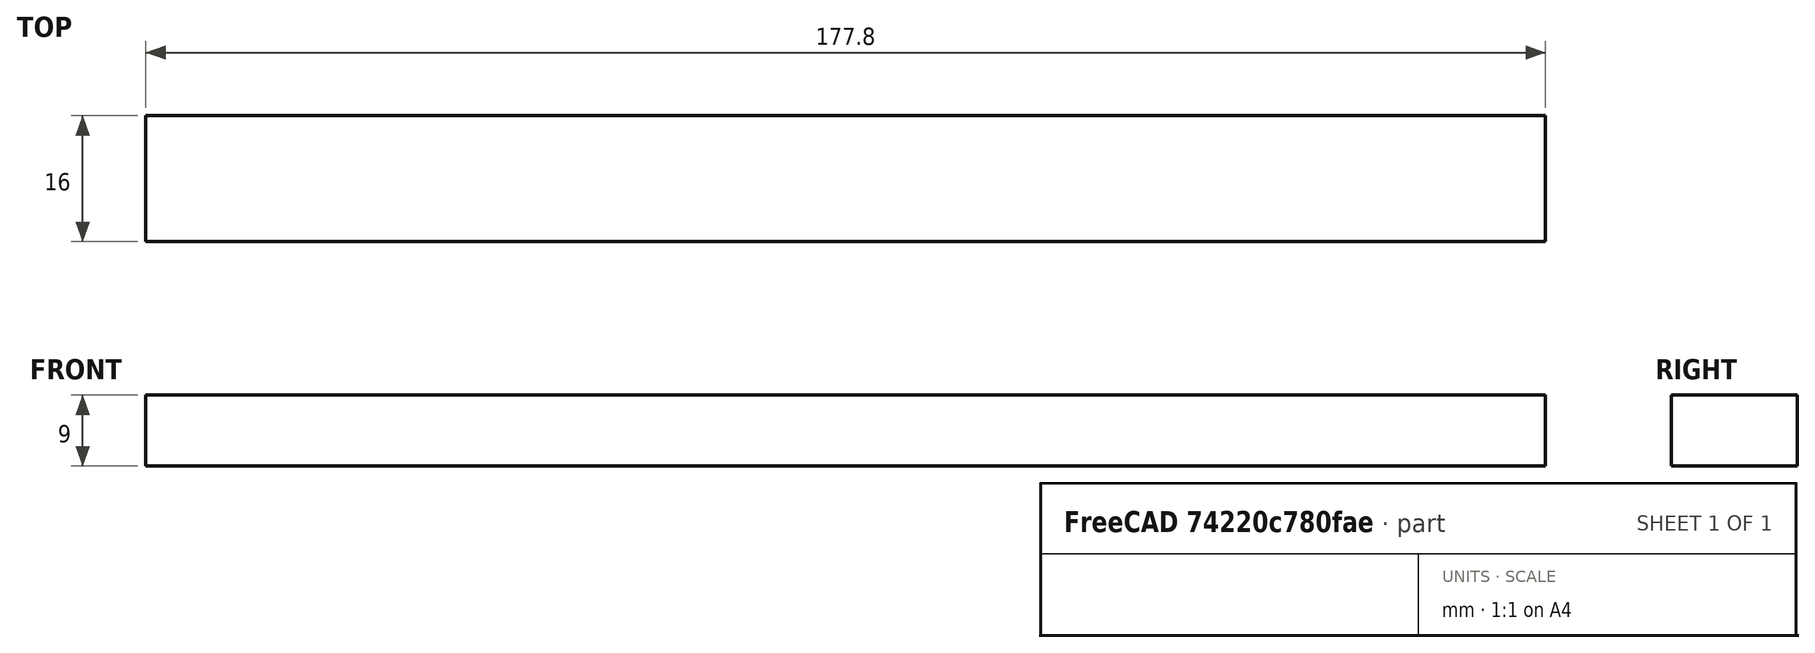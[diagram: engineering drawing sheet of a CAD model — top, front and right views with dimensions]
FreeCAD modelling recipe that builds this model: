
FCSTD DOCUMENT  (FreeCAD 0.17R13543 (Git))
Label: prop_dummy
License: All rights reserved
LicenseURL: http://en.wikipedia.org/wiki/All_rights_reserved
objects: Sketcher::SketchObject×1, PartDesign::Pad×1, PartDesign::Body×1, App::Part×1
note: 4 computed .brp shape members not serialized (recipe doc carries the construction recipe); baked Part::Feature solids carry a one-line shape summary decoded from their .brp

FEATURE [Sketcher::SketchObject] Sketch
  MapMode = 5
  Placement = pos=(0,0,0) rot=(1,0,0;1.5708rad)
  Support = -> [XZ_Plane001]
  sketch-geometry (4):
    g0: LineSegment StartX=-88.9 StartY=-8 StartZ=0 EndX=88.9 EndY=-8 EndZ=0
    g1: LineSegment StartX=88.9 StartY=-8 StartZ=0 EndX=88.9 EndY=8 EndZ=0
    g2: LineSegment StartX=88.9 StartY=8 StartZ=0 EndX=-88.9 EndY=8 EndZ=0
    g3: LineSegment StartX=-88.9 StartY=8 StartZ=0 EndX=-88.9 EndY=-8 EndZ=0
  constraints (11):
    c: Coincident(g0,g1)
    c: Coincident(g1,g2)
    c: Coincident(g2,g3)
    c: Coincident(g3,g0)
    c: Horizontal(g0)
    c: Horizontal(g2)
    c: Vertical(g1)
    c: Vertical(g3)
    c: Symmetric(g0,g1,g-1)
    c: DistanceX(g2,g2) = 177.8
    c: DistanceY(g3,g3) = 16
FEATURE [PartDesign::Pad] Pad
  Length = 9
  Length2 = 100
  Placement = pos=(0,0,0) rot=(1,0,0;1.5708rad)
  Profile = -> Sketch
  Type = 0
FEATURE [PartDesign::Body] Body
  Group = -> [Sketch,Pad]
  Origin = -> Origin001
  Placement = pos=(0,0,-8) rot=(1,0,0;1.5708rad)
  Tip = -> Pad
FEATURE [App::Part] Part
  Group = -> [Body]
  License = CC BY 3.0
  LicenseURL = http://creativecommons.org/licenses/by/3.0/
  Origin = -> Origin
